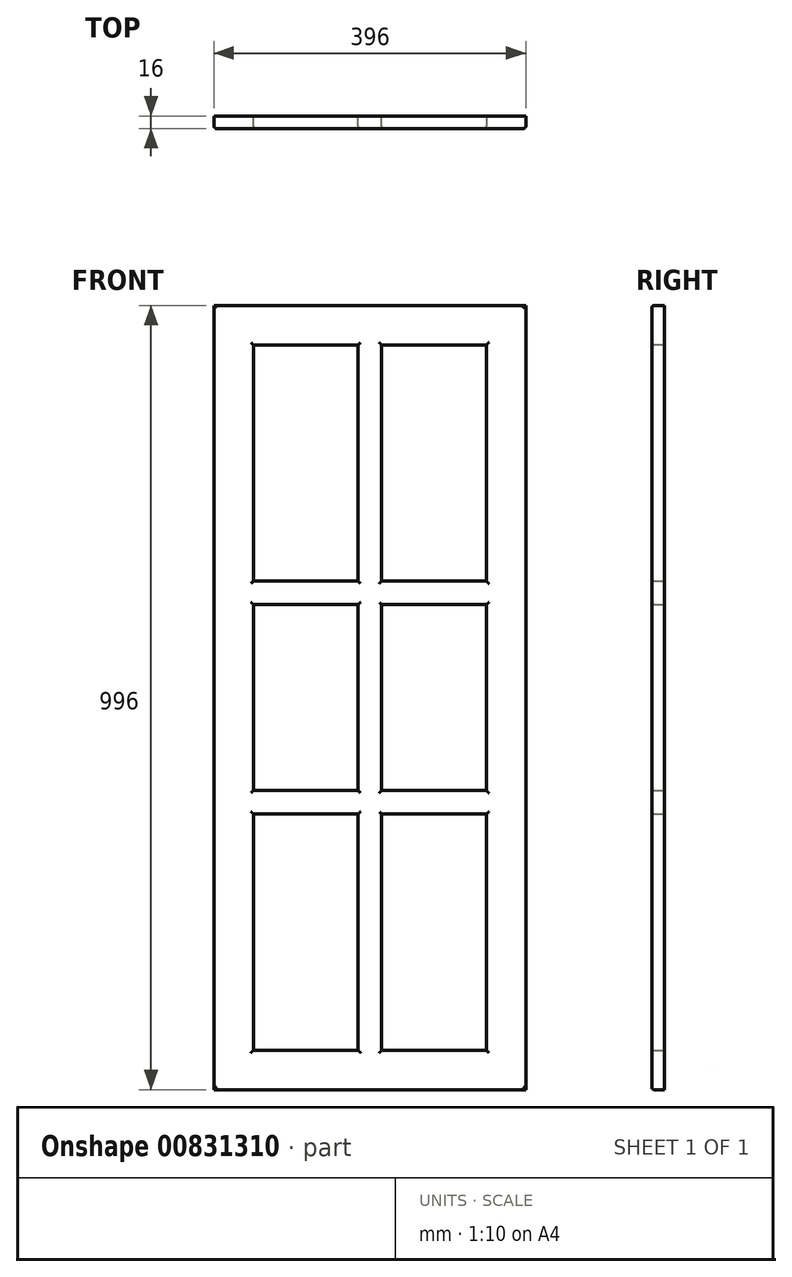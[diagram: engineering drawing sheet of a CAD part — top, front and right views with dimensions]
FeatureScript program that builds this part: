
annotation { "Feature Type Name" : "Feature", "Feature Type Description" : "" }
export const myFeature = defineFeature(function(context is Context, id is Id, definition is map)
    precondition{}
    {
        {
            var Q0;
            Q0=qCreatedBy(makeId("Front.planeOp"),FACE);
            var sketch = newSketch(context, id + "F0", { "sketchPlane" : qUnion([Q0])});
            skLineSegment(sketch, "E0.bottom", {"start": v(0, 0) * mm, "end": v(28.85, 0) * mm});
            skLineSegment(sketch, "E0.top", {"start": v(0, 37.88) * mm, "end": v(28.85, 37.88) * mm});
            skLineSegment(sketch, "E0.left", {"start": v(0, 0) * mm, "end": v(0, 37.88) * mm});
            skLineSegment(sketch, "E0.right", {"start": v(28.85, 0) * mm, "end": v(28.85, 37.88) * mm});
            skSolve(sketch);
        }
        {
            var Q0;
            Q0=makeQuery(id+"F0.imprint","IMPRINT",FACE,{"disambiguationData":[TD([[makeQuery(id+"F0.imprint","IMPRINT",EDGE,{"derivedFrom":sQuery(id+"F0.wireOp",EDGE,"E0.bottom")}),1.0]])]});
            extrude(context, id + "F1", {"entities" : qUnion([Q0]), "depth" : 16 * mm, "offsetDistance" : 25.4 * mm});
        }
        {
            var Q0;
            Q0=makeQuery(id+"F1.opExtrude","SWEPT_FACE",FACE,{"disambiguationData":[OSD([sQuery(id+"F0.wireOp",EDGE,"E0.left")])]});
            extrude(context, id + "F2", {"entities" : qUnion([Q0]), "operationType" : NewBodyOperationType.ADD, "oppositeDirection" : true, "depth" : 296 * mm, "offsetDistance" : 25.4 * mm});
        }
        {
            var Q0;
            {var subQ0=sQuery(id+"F0.wireOp",EDGE,"E0.bottom");Q0=makeQuery(id+"F2.boolean.opBoolean","MERGE",FACE,{"derivedFrom":[makeQuery(id+"F1.opExtrude","SWEPT_FACE",FACE,{"disambiguationData":[OSD([subQ0])]}),makeQuery(id+"F2.opExtrude","SWEPT_FACE",FACE,{"disambiguationData":[OSD([subQ0,sQuery(id+"F0.wireOp",EDGE,"E0.left")])]})]});}
            extrude(context, id + "F3", {"entities" : qUnion([Q0]), "operationType" : NewBodyOperationType.ADD, "oppositeDirection" : true, "depth" : 996 * mm, "offsetDistance" : 25 * mm});
        }
        {
            var Q0;
            {var subQ0=sQuery(id+"F0.wireOp",EDGE,"E0.left");var subQ1=sQuery(id+"F0.wireOp",EDGE,"E0.bottom");Q0=makeQuery(id+"F3.boolean.opBoolean","MERGE",FACE,{"derivedFrom":[makeQuery(id+"F2.boolean.opBoolean","MERGE",FACE,{"derivedFrom":[makeQuery(id+"F1.opExtrude","CAP_FACE",FACE,{"disambiguationData":[OSD([subQ1,sQuery(id+"F0.wireOp",EDGE,"E0.top"),subQ0,sQuery(id+"F0.wireOp",EDGE,"E0.right")])],"isStart":false}),makeQuery(id+"F2.opExtrude","SWEPT_FACE",FACE,{"disambiguationData":[OSD([subQ0]),TDD([makeQuery(id+"F1.opExtrude","CAP_EDGE",EDGE,{"disambiguationData":[OSD([subQ0])],"isStart":false})])]})]}),makeQuery(id+"F3.opExtrude","SWEPT_FACE",FACE,{"disambiguationData":[OSD([subQ1,subQ0]),TDD([makeQuery(id+"F2.boolean.opBoolean","MERGE",EDGE,{"derivedFrom":[makeQuery(id+"F1.opExtrude","CAP_EDGE",EDGE,{"disambiguationData":[OSD([subQ1])],"isStart":false}),makeQuery(id+"F2.opExtrude","SWEPT_EDGE",EDGE,{"disambiguationData":[OSD([subQ1,subQ0]),TDD([makeQuery(id+"F1.opExtrude","CAP_VERTEX",VERTEX,{"disambiguationData":[OSD([subQ1,subQ0])],"isStart":false})])]})]})])]})]});}
            var sketch = newSketch(context, id + "F4", { "sketchPlane" : qUnion([Q0])});
            skLineSegment(sketch, "E1.bottom", {"start": v(48.4, 906.79) * mm, "end": v(248.24, 906.79) * mm});
            skLineSegment(sketch, "E1.top", {"start": v(48.4, 105.66) * mm, "end": v(248.24, 105.66) * mm});
            skLineSegment(sketch, "E1.left", {"start": v(48.4, 906.79) * mm, "end": v(48.4, 105.66) * mm});
            skLineSegment(sketch, "E1.right", {"start": v(248.24, 906.79) * mm, "end": v(248.24, 105.66) * mm});
            skSolve(sketch);
        }
        {
            var Q0;
            Q0=makeQuery(id+"F4.imprint","IMPRINT",FACE,{"disambiguationData":[TD([[makeQuery(id+"F4.imprint","IMPRINT",EDGE,{"derivedFrom":sQuery(id+"F4.wireOp",EDGE,"E1.bottom")}),-1.0]])]});
            extrude(context, id + "F5", {"entities" : qUnion([Q0]), "operationType" : NewBodyOperationType.REMOVE, "oppositeDirection" : true, "depth" : 5 * mm, "offsetDistance" : 25 * mm});
        }
        {
            var Q0;
            Q0=makeQuery(id+"F5.boolean.opBoolean","COPY",FACE,{"derivedFrom":makeQuery(id+"F5.opExtrude","SWEPT_FACE",FACE,{"disambiguationData":[OSD([sQuery(id+"F4.wireOp",EDGE,"E1.bottom")])]})});
            extrude(context, id + "F6", {"entities" : qUnion([Q0]), "operationType" : NewBodyOperationType.REMOVE, "oppositeDirection" : true, "depth" : 39.2 * mm, "offsetDistance" : 25 * mm});
        }
        {
            var Q0;
            {var subQ0=sQuery(id+"F4.wireOp",EDGE,"E1.right");Q0=makeQuery(id+"F6.boolean.opBoolean","MERGE",FACE,{"derivedFrom":[makeQuery(id+"F5.boolean.opBoolean","COPY",FACE,{"derivedFrom":makeQuery(id+"F5.opExtrude","SWEPT_FACE",FACE,{"disambiguationData":[OSD([subQ0])]})}),makeQuery(id+"F6.opExtrude","SWEPT_FACE",FACE,{"disambiguationData":[OSD([sQuery(id+"F4.wireOp",EDGE,"E1.bottom"),subQ0])]})]});}
            extrude(context, id + "F7", {"entities" : qUnion([Q0]), "operationType" : NewBodyOperationType.ADD, "depth" : 2.24 * mm, "offsetDistance" : 25 * mm});
        }
        {
            var Q0;
            Q0=makeQuery(id+"F5.boolean.opBoolean","COPY",FACE,{"derivedFrom":makeQuery(id+"F5.opExtrude","SWEPT_FACE",FACE,{"disambiguationData":[OSD([sQuery(id+"F4.wireOp",EDGE,"E1.top")])]})});
            extrude(context, id + "F8", {"entities" : qUnion([Q0]), "operationType" : NewBodyOperationType.REMOVE, "oppositeDirection" : true, "depth" : 55.66 * mm, "offsetDistance" : 25 * mm});
        }
        {
            var Q0;
            {var subQ0=sQuery(id+"F4.wireOp",EDGE,"E1.left");Q0=makeQuery(id+"F8.boolean.opBoolean","MERGE",FACE,{"derivedFrom":[makeQuery(id+"F6.boolean.opBoolean","MERGE",FACE,{"derivedFrom":[makeQuery(id+"F5.boolean.opBoolean","COPY",FACE,{"derivedFrom":makeQuery(id+"F5.opExtrude","SWEPT_FACE",FACE,{"disambiguationData":[OSD([subQ0])]})}),makeQuery(id+"F6.opExtrude","SWEPT_FACE",FACE,{"disambiguationData":[OSD([sQuery(id+"F4.wireOp",EDGE,"E1.bottom"),subQ0])]})]}),makeQuery(id+"F8.opExtrude","SWEPT_FACE",FACE,{"disambiguationData":[OSD([sQuery(id+"F4.wireOp",EDGE,"E1.top"),subQ0])]})]});}
            extrude(context, id + "F9", {"entities" : qUnion([Q0]), "operationType" : NewBodyOperationType.ADD, "depth" : 1.59 * mm, "offsetDistance" : 25 * mm});
        }
        {
            var Q0;
            {var subQ0=sQuery(id+"F4.wireOp",EDGE,"E1.top");var subQ1=sQuery(id+"F4.wireOp",EDGE,"E1.bottom");Q0=makeQuery(id+"F8.boolean.opBoolean","MERGE",FACE,{"derivedFrom":[makeQuery(id+"F6.boolean.opBoolean","MERGE",FACE,{"derivedFrom":[makeQuery(id+"F5.boolean.opBoolean","COPY",FACE,{"derivedFrom":makeQuery(id+"F5.opExtrude","CAP_FACE",FACE,{"disambiguationData":[OSD([subQ1,subQ0,sQuery(id+"F4.wireOp",EDGE,"E1.left"),sQuery(id+"F4.wireOp",EDGE,"E1.right")])],"isStart":false})}),makeQuery(id+"F6.opExtrude","SWEPT_FACE",FACE,{"disambiguationData":[OSD([subQ1]),TDD([makeQuery(id+"F5.boolean.opBoolean","COPY",EDGE,{"derivedFrom":makeQuery(id+"F5.opExtrude","CAP_EDGE",EDGE,{"disambiguationData":[OSD([subQ1])],"isStart":false})})])]})]}),makeQuery(id+"F8.opExtrude","SWEPT_FACE",FACE,{"disambiguationData":[OSD([subQ0]),TDD([makeQuery(id+"F5.boolean.opBoolean","COPY",EDGE,{"derivedFrom":makeQuery(id+"F5.opExtrude","CAP_EDGE",EDGE,{"disambiguationData":[OSD([subQ0])],"isStart":false})})])]})]});}
            var sketch = newSketch(context, id + "F10", { "sketchPlane" : qUnion([Q0])});
            skLineSegment(sketch, "E2.bottom", {"start": v(127.14, 946) * mm, "end": v(181.91, 946) * mm});
            skLineSegment(sketch, "E2.top", {"start": v(127.14, 50) * mm, "end": v(181.91, 50) * mm});
            skLineSegment(sketch, "E2.left", {"start": v(127.14, 946) * mm, "end": v(127.14, 50) * mm});
            skLineSegment(sketch, "E2.right", {"start": v(181.91, 946) * mm, "end": v(181.91, 50) * mm});
            skSolve(sketch);
        }
        {
            var Q0;
            Q0=makeQuery(id+"F10.imprint","IMPRINT",FACE,{"disambiguationData":[TD([[makeQuery(id+"F10.imprint","IMPRINT",EDGE,{"derivedFrom":sQuery(id+"F10.wireOp",EDGE,"E2.bottom")}),-1.0]])]});
            extrude(context, id + "F11", {"entities" : qUnion([Q0]), "operationType" : NewBodyOperationType.ADD, "depth" : 5 * mm, "offsetDistance" : 25 * mm});
        }
        {
            var Q0;
            Q0=makeQuery(id+"F11.opExtrude","SWEPT_FACE",FACE,{"disambiguationData":[OSD([sQuery(id+"F10.wireOp",EDGE,"E2.left")])]});
            extrude(context, id + "F12", {"entities" : qUnion([Q0]), "operationType" : NewBodyOperationType.REMOVE, "oppositeDirection" : true, "depth" : 5.86 * mm, "offsetDistance" : 25 * mm});
        }
        {
            var Q0;
            Q0=makeQuery(id+"F11.opExtrude","SWEPT_FACE",FACE,{"disambiguationData":[OSD([sQuery(id+"F10.wireOp",EDGE,"E2.right")])]});
            extrude(context, id + "F13", {"entities" : qUnion([Q0]), "operationType" : NewBodyOperationType.REMOVE, "oppositeDirection" : true, "depth" : 18.91 * mm, "offsetDistance" : 25 * mm});
        }
        {
            var Q0;
            {var subQ0=sQuery(id+"F10.wireOp",EDGE,"E2.left");var subQ1=sQuery(id+"F4.wireOp",EDGE,"E1.bottom");var subQ2=sQuery(id+"F4.wireOp",EDGE,"E1.top");var subQ3=sQuery(id+"F4.wireOp",EDGE,"E1.left");Q0=makeQuery(id+"F12.boolean.opBoolean","MERGE",FACE,{"derivedFrom":[makeQuery(id+"F11.boolean.opBoolean","SPLIT",FACE,{"disambiguationData":[TD([makeQuery(id+"F11.opExtrude","SWEPT_FACE",FACE,{"disambiguationData":[OSD([subQ0])]})])],"derivedFrom":makeQuery(id+"F8.boolean.opBoolean","MERGE",FACE,{"derivedFrom":[makeQuery(id+"F6.boolean.opBoolean","MERGE",FACE,{"derivedFrom":[makeQuery(id+"F5.boolean.opBoolean","COPY",FACE,{"derivedFrom":makeQuery(id+"F5.opExtrude","CAP_FACE",FACE,{"disambiguationData":[OSD([subQ1,subQ2,subQ3,sQuery(id+"F4.wireOp",EDGE,"E1.right")])],"isStart":false})}),makeQuery(id+"F6.opExtrude","SWEPT_FACE",FACE,{"disambiguationData":[OSD([subQ1]),TDD([makeQuery(id+"F5.boolean.opBoolean","COPY",EDGE,{"derivedFrom":makeQuery(id+"F5.opExtrude","CAP_EDGE",EDGE,{"disambiguationData":[OSD([subQ1])],"isStart":false})})])]})]}),makeQuery(id+"F8.opExtrude","SWEPT_FACE",FACE,{"disambiguationData":[OSD([subQ2]),TDD([makeQuery(id+"F5.boolean.opBoolean","COPY",EDGE,{"derivedFrom":makeQuery(id+"F5.opExtrude","CAP_EDGE",EDGE,{"disambiguationData":[OSD([subQ2])],"isStart":false})})])]})]})}),makeQuery(id+"F12.opExtrude","SWEPT_FACE",FACE,{"disambiguationData":[OSD([subQ0]),TDD([makeQuery(id+"F11.opExtrude","CAP_EDGE",EDGE,{"disambiguationData":[OSD([subQ0])],"isStart":true})])]})]});}
            var sketch = newSketch(context, id + "F14", { "sketchPlane" : qUnion([Q0])});
            skLineSegment(sketch, "E3.bottom", {"start": v(50, 870.78) * mm, "end": v(133, 870.78) * mm});
            skLineSegment(sketch, "E3.top", {"start": v(50, 835.83) * mm, "end": v(133, 835.83) * mm});
            skLineSegment(sketch, "E3.left", {"start": v(50, 870.78) * mm, "end": v(50, 835.83) * mm});
            skLineSegment(sketch, "E3.right", {"start": v(133, 870.78) * mm, "end": v(133, 835.83) * mm});
            skLineSegment(sketch, "E4.bottom", {"start": v(50, 539.3) * mm, "end": v(133, 539.3) * mm});
            skLineSegment(sketch, "E4.top", {"start": v(50, 484.02) * mm, "end": v(133, 484.02) * mm});
            skLineSegment(sketch, "E4.left", {"start": v(50, 539.3) * mm, "end": v(50, 484.02) * mm});
            skLineSegment(sketch, "E4.right", {"start": v(133, 539.3) * mm, "end": v(133, 484.02) * mm});
            skSolve(sketch);
        }
        {
            var Q0;
            {var subQ0=sQuery(id+"F10.wireOp",EDGE,"E2.right");var subQ1=sQuery(id+"F4.wireOp",EDGE,"E1.top");var subQ2=sQuery(id+"F4.wireOp",EDGE,"E1.right");var subQ3=sQuery(id+"F4.wireOp",EDGE,"E1.bottom");Q0=makeQuery(id+"F13.boolean.opBoolean","MERGE",FACE,{"derivedFrom":[makeQuery(id+"F11.boolean.opBoolean","SPLIT",FACE,{"disambiguationData":[TD([makeQuery(id+"F11.opExtrude","SWEPT_FACE",FACE,{"disambiguationData":[OSD([subQ0])]})])],"derivedFrom":makeQuery(id+"F8.boolean.opBoolean","MERGE",FACE,{"derivedFrom":[makeQuery(id+"F6.boolean.opBoolean","MERGE",FACE,{"derivedFrom":[makeQuery(id+"F5.boolean.opBoolean","COPY",FACE,{"derivedFrom":makeQuery(id+"F5.opExtrude","CAP_FACE",FACE,{"disambiguationData":[OSD([subQ3,subQ1,sQuery(id+"F4.wireOp",EDGE,"E1.left"),subQ2])],"isStart":false})}),makeQuery(id+"F6.opExtrude","SWEPT_FACE",FACE,{"disambiguationData":[OSD([subQ3]),TDD([makeQuery(id+"F5.boolean.opBoolean","COPY",EDGE,{"derivedFrom":makeQuery(id+"F5.opExtrude","CAP_EDGE",EDGE,{"disambiguationData":[OSD([subQ3])],"isStart":false})})])]})]}),makeQuery(id+"F8.opExtrude","SWEPT_FACE",FACE,{"disambiguationData":[OSD([subQ1]),TDD([makeQuery(id+"F5.boolean.opBoolean","COPY",EDGE,{"derivedFrom":makeQuery(id+"F5.opExtrude","CAP_EDGE",EDGE,{"disambiguationData":[OSD([subQ1])],"isStart":false})})])]})]})}),makeQuery(id+"F13.opExtrude","SWEPT_FACE",FACE,{"disambiguationData":[OSD([subQ0]),TDD([makeQuery(id+"F11.opExtrude","CAP_EDGE",EDGE,{"disambiguationData":[OSD([subQ0])],"isStart":true})])]})]});}
            var sketch = newSketch(context, id + "F15", { "sketchPlane" : qUnion([Q0])});
            skLineSegment(sketch, "E5.bottom", {"start": v(163, 876.14) * mm, "end": v(246, 876.14) * mm});
            skLineSegment(sketch, "E5.top", {"start": v(163, 831.26) * mm, "end": v(246, 831.26) * mm});
            skLineSegment(sketch, "E5.left", {"start": v(163, 876.14) * mm, "end": v(163, 831.26) * mm});
            skLineSegment(sketch, "E5.right", {"start": v(246, 876.14) * mm, "end": v(246, 831.26) * mm});
            skLineSegment(sketch, "E6.bottom", {"start": v(163, 602.8) * mm, "end": v(246, 602.8) * mm});
            skLineSegment(sketch, "E6.top", {"start": v(163, 550.28) * mm, "end": v(246, 550.28) * mm});
            skLineSegment(sketch, "E6.left", {"start": v(163, 602.8) * mm, "end": v(163, 550.28) * mm});
            skLineSegment(sketch, "E6.right", {"start": v(246, 602.8) * mm, "end": v(246, 550.28) * mm});
            skSolve(sketch);
        }
        {
            var Q0;
            Q0=makeQuery(id+"F14.imprint","IMPRINT",FACE,{"disambiguationData":[TD([[makeQuery(id+"F14.imprint","IMPRINT",EDGE,{"derivedFrom":sQuery(id+"F14.wireOp",EDGE,"E3.bottom")}),-1.0]])]});
            var Q1;
            Q1=makeQuery(id+"F15.imprint","IMPRINT",FACE,{"disambiguationData":[TD([[makeQuery(id+"F15.imprint","IMPRINT",EDGE,{"derivedFrom":sQuery(id+"F15.wireOp",EDGE,"E5.bottom")}),-1.0]])]});
            var Q2;
            Q2=makeQuery(id+"F15.imprint","IMPRINT",FACE,{"disambiguationData":[TD([[makeQuery(id+"F15.imprint","IMPRINT",EDGE,{"derivedFrom":sQuery(id+"F15.wireOp",EDGE,"E6.bottom")}),-1.0]])]});
            var Q3;
            Q3=makeQuery(id+"F14.imprint","IMPRINT",FACE,{"disambiguationData":[TD([[makeQuery(id+"F14.imprint","IMPRINT",EDGE,{"derivedFrom":sQuery(id+"F14.wireOp",EDGE,"E4.bottom")}),-1.0]])]});
            extrude(context, id + "F16", {"entities" : qUnion([Q0, Q1, Q2, Q3]), "operationType" : NewBodyOperationType.ADD, "depth" : 5 * mm, "offsetDistance" : 25 * mm});
        }
        {
            var Q0;
            Q0=makeQuery(id+"F16.opExtrude","SWEPT_FACE",FACE,{"disambiguationData":[OSD([sQuery(id+"F15.wireOp",EDGE,"E6.top")])]});
            var Q1;
            Q1=makeQuery(id+"F16.opExtrude","SWEPT_FACE",FACE,{"disambiguationData":[OSD([sQuery(id+"F14.wireOp",EDGE,"E4.top")])]});
            extrude(context, id + "F17", {"entities" : qUnion([Q0, Q1]), "operationType" : NewBodyOperationType.ADD, "depth" : 300 * mm, "offsetDistance" : 25 * mm});
        }
        {
            var Q0;
            Q0=makeQuery(id+"F16.opExtrude","SWEPT_FACE",FACE,{"disambiguationData":[OSD([sQuery(id+"F14.wireOp",EDGE,"E4.bottom")])]});
            var Q1;
            Q1=makeQuery(id+"F16.opExtrude","SWEPT_FACE",FACE,{"disambiguationData":[OSD([sQuery(id+"F15.wireOp",EDGE,"E6.bottom")])]});
            extrude(context, id + "F18", {"entities" : qUnion([Q0, Q1]), "operationType" : NewBodyOperationType.REMOVE, "oppositeDirection" : true, "depth" : 300 * mm, "offsetDistance" : 25 * mm});
        }
        {
            var Q0;
            Q0=makeQuery(id+"F16.opExtrude","SWEPT_FACE",FACE,{"disambiguationData":[OSD([sQuery(id+"F14.wireOp",EDGE,"E3.top")])]});
            extrude(context, id + "F19", {"entities" : qUnion([Q0]), "operationType" : NewBodyOperationType.ADD, "depth" : 324.8 * mm, "offsetDistance" : 25 * mm});
        }
        {
            var Q0;
            Q0=makeQuery(id+"F16.opExtrude","SWEPT_FACE",FACE,{"disambiguationData":[OSD([sQuery(id+"F14.wireOp",EDGE,"E3.bottom")])]});
            extrude(context, id + "F20", {"entities" : qUnion([Q0]), "operationType" : NewBodyOperationType.REMOVE, "oppositeDirection" : true, "depth" : 324.8 * mm, "offsetDistance" : 25 * mm});
        }
        {
            var Q0;
            Q0=makeQuery(id+"F18.boolean.opBoolean","COPY",FACE,{"derivedFrom":makeQuery(id+"F18.opExtrude","CAP_FACE",FACE,{"disambiguationData":[OSD([sQuery(id+"F14.wireOp",EDGE,"E4.bottom")])],"isStart":false})});
            extrude(context, id + "F21", {"entities" : qUnion([Q0]), "operationType" : NewBodyOperationType.ADD, "depth" : 250 * mm, "offsetDistance" : 25 * mm});
        }
        {
            var Q0;
            Q0=makeQuery(id+"F17.opExtrude","CAP_FACE",FACE,{"disambiguationData":[OSD([sQuery(id+"F14.wireOp",EDGE,"E4.top")])],"isStart":false});
            extrude(context, id + "F22", {"entities" : qUnion([Q0]), "operationType" : NewBodyOperationType.REMOVE, "oppositeDirection" : true, "depth" : 250 * mm, "offsetDistance" : 25 * mm});
        }
        {
            var Q0;
            Q0=makeQuery(id+"F20.boolean.opBoolean","COPY",FACE,{"derivedFrom":makeQuery(id+"F20.opExtrude","CAP_FACE",FACE,{"disambiguationData":[OSD([sQuery(id+"F14.wireOp",EDGE,"E3.bottom")])],"isStart":false})});
            extrude(context, id + "F23", {"entities" : qUnion([Q0]), "operationType" : NewBodyOperationType.ADD, "depth" : 100 * mm, "offsetDistance" : 25 * mm});
        }
        {
            var Q0;
            Q0=makeQuery(id+"F19.opExtrude","CAP_FACE",FACE,{"disambiguationData":[OSD([sQuery(id+"F14.wireOp",EDGE,"E3.top")])],"isStart":false});
            extrude(context, id + "F24", {"entities" : qUnion([Q0]), "operationType" : NewBodyOperationType.REMOVE, "oppositeDirection" : true, "depth" : 100 * mm, "offsetDistance" : 25 * mm});
        }
        {
            var Q0;
            Q0=makeQuery(id+"F23.opExtrude","CAP_FACE",FACE,{"disambiguationData":[OSD([sQuery(id+"F14.wireOp",EDGE,"E3.bottom")])],"isStart":false});
            extrude(context, id + "F25", {"entities" : qUnion([Q0]), "operationType" : NewBodyOperationType.ADD, "depth" : 50 * mm, "offsetDistance" : 25 * mm});
        }
        {
            var Q0;
            Q0=makeQuery(id+"F24.boolean.opBoolean","COPY",FACE,{"derivedFrom":makeQuery(id+"F24.opExtrude","CAP_FACE",FACE,{"disambiguationData":[OSD([sQuery(id+"F14.wireOp",EDGE,"E3.top")])],"isStart":false})});
            extrude(context, id + "F26", {"entities" : qUnion([Q0]), "operationType" : NewBodyOperationType.REMOVE, "oppositeDirection" : true, "depth" : 50 * mm, "offsetDistance" : 25 * mm});
        }
        {
            var Q0;
            Q0=makeQuery(id+"F22.boolean.opBoolean","COPY",FACE,{"derivedFrom":makeQuery(id+"F22.opExtrude","CAP_FACE",FACE,{"disambiguationData":[OSD([sQuery(id+"F14.wireOp",EDGE,"E4.top")])],"isStart":false})});
            extrude(context, id + "F27", {"entities" : qUnion([Q0]), "operationType" : NewBodyOperationType.ADD, "depth" : 134.02 * mm, "offsetDistance" : 25 * mm});
        }
        {
            var Q0;
            Q0=makeQuery(id+"F27.opExtrude","CAP_FACE",FACE,{"disambiguationData":[OSD([sQuery(id+"F14.wireOp",EDGE,"E4.top")])],"isStart":false});
            extrude(context, id + "F28", {"entities" : qUnion([Q0]), "operationType" : NewBodyOperationType.REMOVE, "oppositeDirection" : true, "depth" : 100 * mm, "offsetDistance" : 25 * mm});
        }
        {
            var Q0;
            Q0=makeQuery(id+"F26.boolean.opBoolean","COPY",FACE,{"derivedFrom":makeQuery(id+"F26.opExtrude","CAP_FACE",FACE,{"disambiguationData":[OSD([sQuery(id+"F14.wireOp",EDGE,"E3.top")])],"isStart":false})});
            extrude(context, id + "F29", {"entities" : qUnion([Q0]), "operationType" : NewBodyOperationType.ADD, "depth" : 100 * mm, "offsetDistance" : 25 * mm});
        }
        {
            var Q0;
            Q0=makeQuery(id+"F25.opExtrude","CAP_FACE",FACE,{"disambiguationData":[OSD([sQuery(id+"F14.wireOp",EDGE,"E3.bottom")])],"isStart":false});
            extrude(context, id + "F30", {"entities" : qUnion([Q0]), "operationType" : NewBodyOperationType.REMOVE, "oppositeDirection" : true, "depth" : 100 * mm, "offsetDistance" : 25 * mm});
        }
        {
            var Q0;
            Q0=makeQuery(id+"F30.boolean.opBoolean","COPY",FACE,{"derivedFrom":makeQuery(id+"F30.opExtrude","CAP_FACE",FACE,{"disambiguationData":[OSD([sQuery(id+"F14.wireOp",EDGE,"E3.bottom")])],"isStart":false})});
            extrude(context, id + "F31", {"entities" : qUnion([Q0]), "operationType" : NewBodyOperationType.ADD, "depth" : 50 * mm, "offsetDistance" : 25 * mm});
        }
        {
            var Q0;
            Q0=makeQuery(id+"F29.opExtrude","CAP_FACE",FACE,{"disambiguationData":[OSD([sQuery(id+"F14.wireOp",EDGE,"E3.top")])],"isStart":false});
            extrude(context, id + "F32", {"entities" : qUnion([Q0]), "operationType" : NewBodyOperationType.REMOVE, "oppositeDirection" : true, "depth" : 54.95 * mm, "offsetDistance" : 25 * mm});
        }
        {
            var Q0;
            Q0=makeQuery(id+"F28.boolean.opBoolean","COPY",FACE,{"derivedFrom":makeQuery(id+"F28.opExtrude","CAP_FACE",FACE,{"disambiguationData":[OSD([sQuery(id+"F14.wireOp",EDGE,"E4.top")])],"isStart":false})});
            extrude(context, id + "F33", {"entities" : qUnion([Q0]), "operationType" : NewBodyOperationType.ADD, "depth" : 50 * mm, "offsetDistance" : 25 * mm});
        }
        {
            var Q0;
            Q0=makeQuery(id+"F21.opExtrude","CAP_FACE",FACE,{"disambiguationData":[OSD([sQuery(id+"F14.wireOp",EDGE,"E4.bottom")])],"isStart":false});
            extrude(context, id + "F34", {"entities" : qUnion([Q0]), "operationType" : NewBodyOperationType.REMOVE, "oppositeDirection" : true, "depth" : 109.3 * mm, "offsetDistance" : 25 * mm});
        }
        {
            var Q0;
            Q0=makeQuery(id+"F16.opExtrude","SWEPT_FACE",FACE,{"disambiguationData":[OSD([sQuery(id+"F15.wireOp",EDGE,"E5.top")])]});
            extrude(context, id + "F35", {"entities" : qUnion([Q0]), "operationType" : NewBodyOperationType.REMOVE, "oppositeDirection" : true, "depth" : 14.88 * mm, "offsetDistance" : 25 * mm});
        }
        {
            var Q0;
            Q0=makeQuery(id+"F35.boolean.opBoolean","COPY",FACE,{"derivedFrom":makeQuery(id+"F35.opExtrude","CAP_FACE",FACE,{"disambiguationData":[OSD([sQuery(id+"F15.wireOp",EDGE,"E5.top")])],"isStart":false})});
            extrude(context, id + "F36", {"entities" : qUnion([Q0]), "operationType" : NewBodyOperationType.ADD, "depth" : 230.15 * mm, "offsetDistance" : 25 * mm});
        }
        {
            var Q0;
            Q0=makeQuery(id+"F16.opExtrude","SWEPT_FACE",FACE,{"disambiguationData":[OSD([sQuery(id+"F15.wireOp",EDGE,"E5.bottom")])]});
            extrude(context, id + "F37", {"entities" : qUnion([Q0]), "operationType" : NewBodyOperationType.REMOVE, "oppositeDirection" : true, "depth" : 230.15 * mm, "offsetDistance" : 25 * mm});
        }
        {
            var Q0;
            Q0=makeQuery(id+"F17.opExtrude","CAP_FACE",FACE,{"disambiguationData":[OSD([sQuery(id+"F15.wireOp",EDGE,"E6.top")])],"isStart":false});
            extrude(context, id + "F38", {"entities" : qUnion([Q0]), "operationType" : NewBodyOperationType.REMOVE, "oppositeDirection" : true, "depth" : 22.52 * mm, "offsetDistance" : 25 * mm});
        }
        {
            var Q0;
            Q0=makeQuery(id+"F18.boolean.opBoolean","COPY",FACE,{"derivedFrom":makeQuery(id+"F18.opExtrude","CAP_FACE",FACE,{"disambiguationData":[OSD([sQuery(id+"F15.wireOp",EDGE,"E6.bottom")])],"isStart":false})});
            extrude(context, id + "F39", {"entities" : qUnion([Q0]), "operationType" : NewBodyOperationType.ADD, "depth" : 77.2 * mm, "offsetDistance" : 25 * mm});
        }
        {
            var Q0;
            Q0=makeQuery(id+"F38.boolean.opBoolean","COPY",FACE,{"derivedFrom":makeQuery(id+"F38.opExtrude","CAP_FACE",FACE,{"disambiguationData":[OSD([sQuery(id+"F15.wireOp",EDGE,"E6.top")])],"isStart":false})});
            extrude(context, id + "F40", {"entities" : qUnion([Q0]), "operationType" : NewBodyOperationType.REMOVE, "oppositeDirection" : true, "depth" : 77.2 * mm, "offsetDistance" : 25 * mm});
        }
        {
            var Q0;
            {var subQ0=sQuery(id+"F14.wireOp",EDGE,"E3.bottom");var subQ1=makeQuery(id+"F16.opExtrude","CAP_EDGE",EDGE,{"disambiguationData":[OSD([subQ0])],"isStart":true});var subQ2=sQuery(id+"F10.wireOp",EDGE,"E2.left");var subQ3=sQuery(id+"F4.wireOp",EDGE,"E1.bottom");var subQ4=sQuery(id+"F4.wireOp",EDGE,"E1.left");var subQ5=sQuery(id+"F4.wireOp",EDGE,"E1.top");var subQ7=makeQuery(id+"F6.boolean.opBoolean","COPY",FACE,{"derivedFrom":makeQuery(id+"F6.opExtrude","CAP_FACE",FACE,{"disambiguationData":[OSD([subQ3])],"isStart":false})});Q0=makeQuery(id+"F30.boolean.opBoolean","MERGE",FACE,{"derivedFrom":[makeQuery(id+"F20.boolean.opBoolean","MERGE",FACE,{"derivedFrom":[makeQuery(id+"F16.boolean.opBoolean","SPLIT",FACE,{"disambiguationData":[TD([subQ7])],"derivedFrom":makeQuery(id+"F12.boolean.opBoolean","MERGE",FACE,{"derivedFrom":[makeQuery(id+"F11.boolean.opBoolean","SPLIT",FACE,{"disambiguationData":[TD([makeQuery(id+"F11.opExtrude","SWEPT_FACE",FACE,{"disambiguationData":[OSD([subQ2])]})])],"derivedFrom":makeQuery(id+"F8.boolean.opBoolean","MERGE",FACE,{"derivedFrom":[makeQuery(id+"F6.boolean.opBoolean","MERGE",FACE,{"derivedFrom":[makeQuery(id+"F5.boolean.opBoolean","COPY",FACE,{"derivedFrom":makeQuery(id+"F5.opExtrude","CAP_FACE",FACE,{"disambiguationData":[OSD([subQ3,subQ5,subQ4,sQuery(id+"F4.wireOp",EDGE,"E1.right")])],"isStart":false})}),makeQuery(id+"F6.opExtrude","SWEPT_FACE",FACE,{"disambiguationData":[OSD([subQ3]),TDD([makeQuery(id+"F5.boolean.opBoolean","COPY",EDGE,{"derivedFrom":makeQuery(id+"F5.opExtrude","CAP_EDGE",EDGE,{"disambiguationData":[OSD([subQ3])],"isStart":false})})])]})]}),makeQuery(id+"F8.opExtrude","SWEPT_FACE",FACE,{"disambiguationData":[OSD([subQ5]),TDD([makeQuery(id+"F5.boolean.opBoolean","COPY",EDGE,{"derivedFrom":makeQuery(id+"F5.opExtrude","CAP_EDGE",EDGE,{"disambiguationData":[OSD([subQ5])],"isStart":false})})])]})]})}),makeQuery(id+"F12.opExtrude","SWEPT_FACE",FACE,{"disambiguationData":[OSD([subQ2]),TDD([makeQuery(id+"F11.opExtrude","CAP_EDGE",EDGE,{"disambiguationData":[OSD([subQ2])],"isStart":true})])]})]})}),makeQuery(id+"F20.opExtrude","SWEPT_FACE",FACE,{"disambiguationData":[OSD([subQ0]),TDD([subQ1])]})]}),makeQuery(id+"F30.opExtrude","SWEPT_FACE",FACE,{"disambiguationData":[OSD([subQ0]),TDD([makeQuery(id+"F25.opExtrude","CAP_EDGE",EDGE,{"disambiguationData":[OSD([subQ0]),TDD([makeQuery(id+"F23.opExtrude","CAP_EDGE",EDGE,{"disambiguationData":[OSD([subQ0]),TDD([makeQuery(id+"F20.boolean.opBoolean","COPY",EDGE,{"derivedFrom":makeQuery(id+"F20.opExtrude","CAP_EDGE",EDGE,{"disambiguationData":[OSD([subQ0]),TDD([subQ1])],"isStart":false})})])],"isStart":false})])],"isStart":false})])]})]});}
            var Q1;
            {var subQ0=sQuery(id+"F15.wireOp",EDGE,"E5.bottom");var subQ1=sQuery(id+"F10.wireOp",EDGE,"E2.right");var subQ2=sQuery(id+"F4.wireOp",EDGE,"E1.bottom");var subQ3=sQuery(id+"F4.wireOp",EDGE,"E1.right");var subQ4=sQuery(id+"F4.wireOp",EDGE,"E1.top");var subQ7=makeQuery(id+"F6.boolean.opBoolean","COPY",FACE,{"derivedFrom":makeQuery(id+"F6.opExtrude","CAP_FACE",FACE,{"disambiguationData":[OSD([subQ2])],"isStart":false})});Q1=makeQuery(id+"F37.boolean.opBoolean","MERGE",FACE,{"derivedFrom":[makeQuery(id+"F16.boolean.opBoolean","SPLIT",FACE,{"disambiguationData":[TD([subQ7])],"derivedFrom":makeQuery(id+"F13.boolean.opBoolean","MERGE",FACE,{"derivedFrom":[makeQuery(id+"F11.boolean.opBoolean","SPLIT",FACE,{"disambiguationData":[TD([makeQuery(id+"F11.opExtrude","SWEPT_FACE",FACE,{"disambiguationData":[OSD([subQ1])]})])],"derivedFrom":makeQuery(id+"F8.boolean.opBoolean","MERGE",FACE,{"derivedFrom":[makeQuery(id+"F6.boolean.opBoolean","MERGE",FACE,{"derivedFrom":[makeQuery(id+"F5.boolean.opBoolean","COPY",FACE,{"derivedFrom":makeQuery(id+"F5.opExtrude","CAP_FACE",FACE,{"disambiguationData":[OSD([subQ2,subQ4,sQuery(id+"F4.wireOp",EDGE,"E1.left"),subQ3])],"isStart":false})}),makeQuery(id+"F6.opExtrude","SWEPT_FACE",FACE,{"disambiguationData":[OSD([subQ2]),TDD([makeQuery(id+"F5.boolean.opBoolean","COPY",EDGE,{"derivedFrom":makeQuery(id+"F5.opExtrude","CAP_EDGE",EDGE,{"disambiguationData":[OSD([subQ2])],"isStart":false})})])]})]}),makeQuery(id+"F8.opExtrude","SWEPT_FACE",FACE,{"disambiguationData":[OSD([subQ4]),TDD([makeQuery(id+"F5.boolean.opBoolean","COPY",EDGE,{"derivedFrom":makeQuery(id+"F5.opExtrude","CAP_EDGE",EDGE,{"disambiguationData":[OSD([subQ4])],"isStart":false})})])]})]})}),makeQuery(id+"F13.opExtrude","SWEPT_FACE",FACE,{"disambiguationData":[OSD([subQ1]),TDD([makeQuery(id+"F11.opExtrude","CAP_EDGE",EDGE,{"disambiguationData":[OSD([subQ1])],"isStart":true})])]})]})}),makeQuery(id+"F37.opExtrude","SWEPT_FACE",FACE,{"disambiguationData":[OSD([subQ0]),TDD([makeQuery(id+"F16.opExtrude","CAP_EDGE",EDGE,{"disambiguationData":[OSD([subQ0])],"isStart":true})])]})]});}
            var Q2;
            {var subQ0=sQuery(id+"F15.wireOp",EDGE,"E5.top");var subQ1=sQuery(id+"F15.wireOp",EDGE,"E6.bottom");var subQ2=sQuery(id+"F10.wireOp",EDGE,"E2.right");var subQ3=sQuery(id+"F4.wireOp",EDGE,"E1.right");var subQ4=sQuery(id+"F4.wireOp",EDGE,"E1.top");var subQ6=sQuery(id+"F4.wireOp",EDGE,"E1.bottom");Q2=makeQuery(id+"F35.boolean.opBoolean","MERGE",FACE,{"derivedFrom":[makeQuery(id+"F18.boolean.opBoolean","MERGE",FACE,{"derivedFrom":[makeQuery(id+"F16.boolean.opBoolean","SPLIT",FACE,{"disambiguationData":[TD([makeQuery(id+"F16.opExtrude","SWEPT_FACE",FACE,{"disambiguationData":[OSD([subQ0])]})])],"derivedFrom":makeQuery(id+"F13.boolean.opBoolean","MERGE",FACE,{"derivedFrom":[makeQuery(id+"F11.boolean.opBoolean","SPLIT",FACE,{"disambiguationData":[TD([makeQuery(id+"F11.opExtrude","SWEPT_FACE",FACE,{"disambiguationData":[OSD([subQ2])]})])],"derivedFrom":makeQuery(id+"F8.boolean.opBoolean","MERGE",FACE,{"derivedFrom":[makeQuery(id+"F6.boolean.opBoolean","MERGE",FACE,{"derivedFrom":[makeQuery(id+"F5.boolean.opBoolean","COPY",FACE,{"derivedFrom":makeQuery(id+"F5.opExtrude","CAP_FACE",FACE,{"disambiguationData":[OSD([subQ6,subQ4,sQuery(id+"F4.wireOp",EDGE,"E1.left"),subQ3])],"isStart":false})}),makeQuery(id+"F6.opExtrude","SWEPT_FACE",FACE,{"disambiguationData":[OSD([subQ6]),TDD([makeQuery(id+"F5.boolean.opBoolean","COPY",EDGE,{"derivedFrom":makeQuery(id+"F5.opExtrude","CAP_EDGE",EDGE,{"disambiguationData":[OSD([subQ6])],"isStart":false})})])]})]}),makeQuery(id+"F8.opExtrude","SWEPT_FACE",FACE,{"disambiguationData":[OSD([subQ4]),TDD([makeQuery(id+"F5.boolean.opBoolean","COPY",EDGE,{"derivedFrom":makeQuery(id+"F5.opExtrude","CAP_EDGE",EDGE,{"disambiguationData":[OSD([subQ4])],"isStart":false})})])]})]})}),makeQuery(id+"F13.opExtrude","SWEPT_FACE",FACE,{"disambiguationData":[OSD([subQ2]),TDD([makeQuery(id+"F11.opExtrude","CAP_EDGE",EDGE,{"disambiguationData":[OSD([subQ2])],"isStart":true})])]})]})}),makeQuery(id+"F18.opExtrude","SWEPT_FACE",FACE,{"disambiguationData":[OSD([subQ1]),TDD([makeQuery(id+"F16.opExtrude","CAP_EDGE",EDGE,{"disambiguationData":[OSD([subQ1])],"isStart":true})])]})]}),makeQuery(id+"F35.opExtrude","SWEPT_FACE",FACE,{"disambiguationData":[OSD([subQ0]),TDD([makeQuery(id+"F16.opExtrude","CAP_EDGE",EDGE,{"disambiguationData":[OSD([subQ0])],"isStart":true})])]})]});}
            var Q3;
            {var subQ0=sQuery(id+"F14.wireOp",EDGE,"E4.bottom");var subQ1=makeQuery(id+"F16.opExtrude","CAP_EDGE",EDGE,{"disambiguationData":[OSD([subQ0])],"isStart":true});var subQ2=sQuery(id+"F14.wireOp",EDGE,"E3.top");var subQ3=makeQuery(id+"F19.opExtrude","CAP_EDGE",EDGE,{"disambiguationData":[OSD([subQ2]),TDD([makeQuery(id+"F16.opExtrude","CAP_EDGE",EDGE,{"disambiguationData":[OSD([subQ2])],"isStart":true})])],"isStart":false});var subQ4=makeQuery(id+"F24.boolean.opBoolean","COPY",EDGE,{"derivedFrom":makeQuery(id+"F24.opExtrude","CAP_EDGE",EDGE,{"disambiguationData":[OSD([subQ2]),TDD([subQ3])],"isStart":false})});var subQ5=sQuery(id+"F4.wireOp",EDGE,"E1.left");var subQ6=sQuery(id+"F4.wireOp",EDGE,"E1.top");var subQ7=sQuery(id+"F4.wireOp",EDGE,"E1.bottom");var subQ9=sQuery(id+"F10.wireOp",EDGE,"E2.left");Q3=makeQuery(id+"F34.boolean.opBoolean","MERGE",FACE,{"derivedFrom":[makeQuery(id+"F32.boolean.opBoolean","MERGE",FACE,{"derivedFrom":[makeQuery(id+"F26.boolean.opBoolean","MERGE",FACE,{"derivedFrom":[makeQuery(id+"F24.boolean.opBoolean","MERGE",FACE,{"derivedFrom":[makeQuery(id+"F18.boolean.opBoolean","MERGE",FACE,{"derivedFrom":[makeQuery(id+"F16.boolean.opBoolean","SPLIT",FACE,{"disambiguationData":[TD([makeQuery(id+"F16.opExtrude","SWEPT_FACE",FACE,{"disambiguationData":[OSD([subQ2])]})])],"derivedFrom":makeQuery(id+"F12.boolean.opBoolean","MERGE",FACE,{"derivedFrom":[makeQuery(id+"F11.boolean.opBoolean","SPLIT",FACE,{"disambiguationData":[TD([makeQuery(id+"F11.opExtrude","SWEPT_FACE",FACE,{"disambiguationData":[OSD([subQ9])]})])],"derivedFrom":makeQuery(id+"F8.boolean.opBoolean","MERGE",FACE,{"derivedFrom":[makeQuery(id+"F6.boolean.opBoolean","MERGE",FACE,{"derivedFrom":[makeQuery(id+"F5.boolean.opBoolean","COPY",FACE,{"derivedFrom":makeQuery(id+"F5.opExtrude","CAP_FACE",FACE,{"disambiguationData":[OSD([subQ7,subQ6,subQ5,sQuery(id+"F4.wireOp",EDGE,"E1.right")])],"isStart":false})}),makeQuery(id+"F6.opExtrude","SWEPT_FACE",FACE,{"disambiguationData":[OSD([subQ7]),TDD([makeQuery(id+"F5.boolean.opBoolean","COPY",EDGE,{"derivedFrom":makeQuery(id+"F5.opExtrude","CAP_EDGE",EDGE,{"disambiguationData":[OSD([subQ7])],"isStart":false})})])]})]}),makeQuery(id+"F8.opExtrude","SWEPT_FACE",FACE,{"disambiguationData":[OSD([subQ6]),TDD([makeQuery(id+"F5.boolean.opBoolean","COPY",EDGE,{"derivedFrom":makeQuery(id+"F5.opExtrude","CAP_EDGE",EDGE,{"disambiguationData":[OSD([subQ6])],"isStart":false})})])]})]})}),makeQuery(id+"F12.opExtrude","SWEPT_FACE",FACE,{"disambiguationData":[OSD([subQ9]),TDD([makeQuery(id+"F11.opExtrude","CAP_EDGE",EDGE,{"disambiguationData":[OSD([subQ9])],"isStart":true})])]})]})}),makeQuery(id+"F18.opExtrude","SWEPT_FACE",FACE,{"disambiguationData":[OSD([subQ0]),TDD([subQ1])]})]}),makeQuery(id+"F24.opExtrude","SWEPT_FACE",FACE,{"disambiguationData":[OSD([subQ2]),TDD([subQ3])]})]}),makeQuery(id+"F26.opExtrude","SWEPT_FACE",FACE,{"disambiguationData":[OSD([subQ2]),TDD([subQ4])]})]}),makeQuery(id+"F32.opExtrude","SWEPT_FACE",FACE,{"disambiguationData":[OSD([subQ2]),TDD([makeQuery(id+"F29.opExtrude","CAP_EDGE",EDGE,{"disambiguationData":[OSD([subQ2]),TDD([makeQuery(id+"F26.boolean.opBoolean","COPY",EDGE,{"derivedFrom":makeQuery(id+"F26.opExtrude","CAP_EDGE",EDGE,{"disambiguationData":[OSD([subQ2]),TDD([subQ4])],"isStart":false})})])],"isStart":false})])]})]}),makeQuery(id+"F34.opExtrude","SWEPT_FACE",FACE,{"disambiguationData":[OSD([subQ0]),TDD([makeQuery(id+"F21.opExtrude","CAP_EDGE",EDGE,{"disambiguationData":[OSD([subQ0]),TDD([makeQuery(id+"F18.boolean.opBoolean","COPY",EDGE,{"derivedFrom":makeQuery(id+"F18.opExtrude","CAP_EDGE",EDGE,{"disambiguationData":[OSD([subQ0]),TDD([subQ1])],"isStart":false})})])],"isStart":false})])]})]});}
            var Q4;
            {var subQ0=sQuery(id+"F14.wireOp",EDGE,"E4.top");var subQ1=makeQuery(id+"F17.opExtrude","CAP_EDGE",EDGE,{"disambiguationData":[OSD([subQ0]),TDD([makeQuery(id+"F16.opExtrude","CAP_EDGE",EDGE,{"disambiguationData":[OSD([subQ0])],"isStart":true})])],"isStart":false});var subQ2=sQuery(id+"F10.wireOp",EDGE,"E2.left");var subQ3=sQuery(id+"F4.wireOp",EDGE,"E1.top");var subQ4=sQuery(id+"F4.wireOp",EDGE,"E1.left");var subQ5=sQuery(id+"F4.wireOp",EDGE,"E1.bottom");var subQ7=makeQuery(id+"F8.boolean.opBoolean","COPY",FACE,{"derivedFrom":makeQuery(id+"F8.opExtrude","CAP_FACE",FACE,{"disambiguationData":[OSD([subQ3])],"isStart":false})});Q4=makeQuery(id+"F28.boolean.opBoolean","MERGE",FACE,{"derivedFrom":[makeQuery(id+"F22.boolean.opBoolean","MERGE",FACE,{"derivedFrom":[makeQuery(id+"F16.boolean.opBoolean","SPLIT",FACE,{"disambiguationData":[TD([subQ7])],"derivedFrom":makeQuery(id+"F12.boolean.opBoolean","MERGE",FACE,{"derivedFrom":[makeQuery(id+"F11.boolean.opBoolean","SPLIT",FACE,{"disambiguationData":[TD([makeQuery(id+"F11.opExtrude","SWEPT_FACE",FACE,{"disambiguationData":[OSD([subQ2])]})])],"derivedFrom":makeQuery(id+"F8.boolean.opBoolean","MERGE",FACE,{"derivedFrom":[makeQuery(id+"F6.boolean.opBoolean","MERGE",FACE,{"derivedFrom":[makeQuery(id+"F5.boolean.opBoolean","COPY",FACE,{"derivedFrom":makeQuery(id+"F5.opExtrude","CAP_FACE",FACE,{"disambiguationData":[OSD([subQ5,subQ3,subQ4,sQuery(id+"F4.wireOp",EDGE,"E1.right")])],"isStart":false})}),makeQuery(id+"F6.opExtrude","SWEPT_FACE",FACE,{"disambiguationData":[OSD([subQ5]),TDD([makeQuery(id+"F5.boolean.opBoolean","COPY",EDGE,{"derivedFrom":makeQuery(id+"F5.opExtrude","CAP_EDGE",EDGE,{"disambiguationData":[OSD([subQ5])],"isStart":false})})])]})]}),makeQuery(id+"F8.opExtrude","SWEPT_FACE",FACE,{"disambiguationData":[OSD([subQ3]),TDD([makeQuery(id+"F5.boolean.opBoolean","COPY",EDGE,{"derivedFrom":makeQuery(id+"F5.opExtrude","CAP_EDGE",EDGE,{"disambiguationData":[OSD([subQ3])],"isStart":false})})])]})]})}),makeQuery(id+"F12.opExtrude","SWEPT_FACE",FACE,{"disambiguationData":[OSD([subQ2]),TDD([makeQuery(id+"F11.opExtrude","CAP_EDGE",EDGE,{"disambiguationData":[OSD([subQ2])],"isStart":true})])]})]})}),makeQuery(id+"F22.opExtrude","SWEPT_FACE",FACE,{"disambiguationData":[OSD([subQ0]),TDD([subQ1])]})]}),makeQuery(id+"F28.opExtrude","SWEPT_FACE",FACE,{"disambiguationData":[OSD([subQ0]),TDD([makeQuery(id+"F27.opExtrude","CAP_EDGE",EDGE,{"disambiguationData":[OSD([subQ0]),TDD([makeQuery(id+"F22.boolean.opBoolean","COPY",EDGE,{"derivedFrom":makeQuery(id+"F22.opExtrude","CAP_EDGE",EDGE,{"disambiguationData":[OSD([subQ0]),TDD([subQ1])],"isStart":false})})])],"isStart":false})])]})]});}
            var Q5;
            {var subQ0=sQuery(id+"F15.wireOp",EDGE,"E6.top");var subQ1=makeQuery(id+"F17.opExtrude","CAP_EDGE",EDGE,{"disambiguationData":[OSD([subQ0]),TDD([makeQuery(id+"F16.opExtrude","CAP_EDGE",EDGE,{"disambiguationData":[OSD([subQ0])],"isStart":true})])],"isStart":false});var subQ2=sQuery(id+"F10.wireOp",EDGE,"E2.right");var subQ3=sQuery(id+"F4.wireOp",EDGE,"E1.top");var subQ4=makeQuery(id+"F8.boolean.opBoolean","COPY",FACE,{"derivedFrom":makeQuery(id+"F8.opExtrude","CAP_FACE",FACE,{"disambiguationData":[OSD([subQ3])],"isStart":false})});var subQ5=sQuery(id+"F4.wireOp",EDGE,"E1.right");var subQ7=sQuery(id+"F4.wireOp",EDGE,"E1.bottom");Q5=makeQuery(id+"F40.boolean.opBoolean","MERGE",FACE,{"derivedFrom":[makeQuery(id+"F38.boolean.opBoolean","MERGE",FACE,{"derivedFrom":[makeQuery(id+"F16.boolean.opBoolean","SPLIT",FACE,{"disambiguationData":[TD([subQ4])],"derivedFrom":makeQuery(id+"F13.boolean.opBoolean","MERGE",FACE,{"derivedFrom":[makeQuery(id+"F11.boolean.opBoolean","SPLIT",FACE,{"disambiguationData":[TD([makeQuery(id+"F11.opExtrude","SWEPT_FACE",FACE,{"disambiguationData":[OSD([subQ2])]})])],"derivedFrom":makeQuery(id+"F8.boolean.opBoolean","MERGE",FACE,{"derivedFrom":[makeQuery(id+"F6.boolean.opBoolean","MERGE",FACE,{"derivedFrom":[makeQuery(id+"F5.boolean.opBoolean","COPY",FACE,{"derivedFrom":makeQuery(id+"F5.opExtrude","CAP_FACE",FACE,{"disambiguationData":[OSD([subQ7,subQ3,sQuery(id+"F4.wireOp",EDGE,"E1.left"),subQ5])],"isStart":false})}),makeQuery(id+"F6.opExtrude","SWEPT_FACE",FACE,{"disambiguationData":[OSD([subQ7]),TDD([makeQuery(id+"F5.boolean.opBoolean","COPY",EDGE,{"derivedFrom":makeQuery(id+"F5.opExtrude","CAP_EDGE",EDGE,{"disambiguationData":[OSD([subQ7])],"isStart":false})})])]})]}),makeQuery(id+"F8.opExtrude","SWEPT_FACE",FACE,{"disambiguationData":[OSD([subQ3]),TDD([makeQuery(id+"F5.boolean.opBoolean","COPY",EDGE,{"derivedFrom":makeQuery(id+"F5.opExtrude","CAP_EDGE",EDGE,{"disambiguationData":[OSD([subQ3])],"isStart":false})})])]})]})}),makeQuery(id+"F13.opExtrude","SWEPT_FACE",FACE,{"disambiguationData":[OSD([subQ2]),TDD([makeQuery(id+"F11.opExtrude","CAP_EDGE",EDGE,{"disambiguationData":[OSD([subQ2])],"isStart":true})])]})]})}),makeQuery(id+"F38.opExtrude","SWEPT_FACE",FACE,{"disambiguationData":[OSD([subQ0]),TDD([subQ1])]})]}),makeQuery(id+"F40.opExtrude","SWEPT_FACE",FACE,{"disambiguationData":[OSD([subQ0]),TDD([makeQuery(id+"F38.boolean.opBoolean","COPY",EDGE,{"derivedFrom":makeQuery(id+"F38.opExtrude","CAP_EDGE",EDGE,{"disambiguationData":[OSD([subQ0]),TDD([subQ1])],"isStart":false})})])]})]});}
            extrude(context, id + "F41", {"entities" : qUnion([Q0, Q1, Q2, Q3, Q4, Q5]), "operationType" : NewBodyOperationType.REMOVE, "oppositeDirection" : true, "depth" : 11 * mm, "offsetDistance" : 25 * mm});
        }
        {
            var Q0;
            {var subQ0=sQuery(id+"F0.wireOp",EDGE,"E0.left");var subQ1=sQuery(id+"F0.wireOp",EDGE,"E0.bottom");Q0=makeQuery(id+"F3.boolean.opBoolean","MERGE",FACE,{"derivedFrom":[makeQuery(id+"F2.opExtrude","CAP_FACE",FACE,{"disambiguationData":[OSD([subQ0])],"isStart":false}),makeQuery(id+"F3.opExtrude","SWEPT_FACE",FACE,{"disambiguationData":[OSD([subQ1,subQ0]),TDD([makeQuery(id+"F2.opExtrude","CAP_EDGE",EDGE,{"disambiguationData":[OSD([subQ1,subQ0])],"isStart":false})])]})]});}
            extrude(context, id + "F42", {"entities" : qUnion([Q0]), "operationType" : NewBodyOperationType.ADD, "depth" : 100 * mm, "offsetDistance" : 25 * mm});
        }
        {
            var Q0;
            {var subQ0=sQuery(id+"F15.wireOp",EDGE,"E5.right");var subQ1=sQuery(id+"F15.wireOp",EDGE,"E5.bottom");var subQ2=sQuery(id+"F4.wireOp",EDGE,"E1.right");var subQ3=sQuery(id+"F4.wireOp",EDGE,"E1.top");var subQ4=sQuery(id+"F4.wireOp",EDGE,"E1.bottom");Q0=makeQuery(id+"F41.boolean.opBoolean","MERGE",FACE,{"derivedFrom":[makeQuery(id+"F37.boolean.opBoolean","MERGE",FACE,{"derivedFrom":[makeQuery(id+"F16.boolean.opBoolean","SPLIT",FACE,{"disambiguationData":[TD([makeQuery(id+"F6.boolean.opBoolean","COPY",FACE,{"derivedFrom":makeQuery(id+"F6.opExtrude","CAP_FACE",FACE,{"disambiguationData":[OSD([subQ4])],"isStart":false})})])],"derivedFrom":makeQuery(id+"F8.boolean.opBoolean","MERGE",FACE,{"derivedFrom":[makeQuery(id+"F7.opExtrude","CAP_FACE",FACE,{"disambiguationData":[OSD([subQ4,subQ2])],"isStart":false}),makeQuery(id+"F8.opExtrude","SWEPT_FACE",FACE,{"disambiguationData":[OSD([subQ3,subQ2])]})]})}),makeQuery(id+"F37.opExtrude","SWEPT_FACE",FACE,{"disambiguationData":[OSD([subQ4,subQ3,subQ2,subQ1,subQ0])]})]}),makeQuery(id+"F41.opExtrude","SWEPT_FACE",FACE,{"disambiguationData":[OSD([subQ4,subQ3,subQ2,subQ1,subQ0])]})]});}
            var Q1;
            {var subQ0=sQuery(id+"F15.wireOp",EDGE,"E6.right");var subQ1=sQuery(id+"F15.wireOp",EDGE,"E6.bottom");var subQ2=sQuery(id+"F15.wireOp",EDGE,"E5.right");var subQ3=sQuery(id+"F15.wireOp",EDGE,"E5.top");var subQ4=sQuery(id+"F4.wireOp",EDGE,"E1.right");var subQ5=sQuery(id+"F4.wireOp",EDGE,"E1.top");var subQ6=sQuery(id+"F4.wireOp",EDGE,"E1.bottom");Q1=makeQuery(id+"F41.boolean.opBoolean","MERGE",FACE,{"derivedFrom":[makeQuery(id+"F35.boolean.opBoolean","MERGE",FACE,{"derivedFrom":[makeQuery(id+"F18.boolean.opBoolean","MERGE",FACE,{"derivedFrom":[makeQuery(id+"F16.boolean.opBoolean","SPLIT",FACE,{"disambiguationData":[TD([makeQuery(id+"F16.opExtrude","SWEPT_FACE",FACE,{"disambiguationData":[OSD([subQ3])]})])],"derivedFrom":makeQuery(id+"F8.boolean.opBoolean","MERGE",FACE,{"derivedFrom":[makeQuery(id+"F7.opExtrude","CAP_FACE",FACE,{"disambiguationData":[OSD([subQ6,subQ4])],"isStart":false}),makeQuery(id+"F8.opExtrude","SWEPT_FACE",FACE,{"disambiguationData":[OSD([subQ5,subQ4])]})]})}),makeQuery(id+"F18.opExtrude","SWEPT_FACE",FACE,{"disambiguationData":[OSD([subQ6,subQ5,subQ4,subQ1,subQ0])]})]}),makeQuery(id+"F35.opExtrude","SWEPT_FACE",FACE,{"disambiguationData":[OSD([subQ6,subQ5,subQ4,subQ3,subQ2])]})]}),makeQuery(id+"F41.opExtrude","SWEPT_FACE",FACE,{"disambiguationData":[OSD([subQ6,subQ5,subQ4,subQ3,subQ2,subQ1,subQ0])]})]});}
            var Q2;
            {var subQ0=sQuery(id+"F15.wireOp",EDGE,"E6.right");var subQ1=sQuery(id+"F15.wireOp",EDGE,"E6.top");var subQ2=sQuery(id+"F4.wireOp",EDGE,"E1.right");var subQ3=sQuery(id+"F4.wireOp",EDGE,"E1.top");var subQ4=sQuery(id+"F4.wireOp",EDGE,"E1.bottom");Q2=makeQuery(id+"F41.boolean.opBoolean","MERGE",FACE,{"derivedFrom":[makeQuery(id+"F40.boolean.opBoolean","MERGE",FACE,{"derivedFrom":[makeQuery(id+"F38.boolean.opBoolean","MERGE",FACE,{"derivedFrom":[makeQuery(id+"F16.boolean.opBoolean","SPLIT",FACE,{"disambiguationData":[TD([makeQuery(id+"F8.boolean.opBoolean","COPY",FACE,{"derivedFrom":makeQuery(id+"F8.opExtrude","CAP_FACE",FACE,{"disambiguationData":[OSD([subQ3])],"isStart":false})})])],"derivedFrom":makeQuery(id+"F8.boolean.opBoolean","MERGE",FACE,{"derivedFrom":[makeQuery(id+"F7.opExtrude","CAP_FACE",FACE,{"disambiguationData":[OSD([subQ4,subQ2])],"isStart":false}),makeQuery(id+"F8.opExtrude","SWEPT_FACE",FACE,{"disambiguationData":[OSD([subQ3,subQ2])]})]})}),makeQuery(id+"F38.opExtrude","SWEPT_FACE",FACE,{"disambiguationData":[OSD([subQ4,subQ3,subQ2,subQ1,subQ0])]})]}),makeQuery(id+"F40.opExtrude","SWEPT_FACE",FACE,{"disambiguationData":[OSD([subQ4,subQ3,subQ2,subQ1,subQ0])]})]}),makeQuery(id+"F41.opExtrude","SWEPT_FACE",FACE,{"disambiguationData":[OSD([subQ4,subQ3,subQ2,subQ1,subQ0])]})]});}
            extrude(context, id + "F43", {"entities" : qUnion([Q0, Q1, Q2]), "operationType" : NewBodyOperationType.REMOVE, "oppositeDirection" : true, "depth" : 100 * mm, "offsetDistance" : 25 * mm});
        }
        {
            var Q0;
            {var subQ0=sQuery(id+"F15.wireOp",EDGE,"E5.left");var subQ1=sQuery(id+"F15.wireOp",EDGE,"E5.bottom");var subQ2=sQuery(id+"F10.wireOp",EDGE,"E2.right");var subQ6=sQuery(id+"F4.wireOp",EDGE,"E1.bottom");Q0=makeQuery(id+"F41.boolean.opBoolean","MERGE",FACE,{"derivedFrom":[makeQuery(id+"F37.boolean.opBoolean","MERGE",FACE,{"derivedFrom":[makeQuery(id+"F16.boolean.opBoolean","SPLIT",FACE,{"disambiguationData":[TD([makeQuery(id+"F6.boolean.opBoolean","COPY",FACE,{"derivedFrom":makeQuery(id+"F6.opExtrude","CAP_FACE",FACE,{"disambiguationData":[OSD([subQ6])],"isStart":false})})])],"derivedFrom":makeQuery(id+"F13.boolean.opBoolean","COPY",FACE,{"derivedFrom":makeQuery(id+"F13.opExtrude","CAP_FACE",FACE,{"disambiguationData":[OSD([subQ2])],"isStart":false})})}),makeQuery(id+"F37.opExtrude","SWEPT_FACE",FACE,{"disambiguationData":[OSD([subQ2,subQ1,subQ0])]})]}),makeQuery(id+"F41.opExtrude","SWEPT_FACE",FACE,{"disambiguationData":[OSD([subQ2,subQ1,subQ0])]})]});}
            var Q1;
            {var subQ0=sQuery(id+"F15.wireOp",EDGE,"E6.left");var subQ1=sQuery(id+"F15.wireOp",EDGE,"E6.bottom");var subQ2=sQuery(id+"F15.wireOp",EDGE,"E5.left");var subQ3=sQuery(id+"F15.wireOp",EDGE,"E5.top");var subQ4=sQuery(id+"F10.wireOp",EDGE,"E2.right");Q1=makeQuery(id+"F41.boolean.opBoolean","MERGE",FACE,{"derivedFrom":[makeQuery(id+"F35.boolean.opBoolean","MERGE",FACE,{"derivedFrom":[makeQuery(id+"F18.boolean.opBoolean","MERGE",FACE,{"derivedFrom":[makeQuery(id+"F16.boolean.opBoolean","SPLIT",FACE,{"disambiguationData":[TD([makeQuery(id+"F16.opExtrude","SWEPT_FACE",FACE,{"disambiguationData":[OSD([subQ3])]})])],"derivedFrom":makeQuery(id+"F13.boolean.opBoolean","COPY",FACE,{"derivedFrom":makeQuery(id+"F13.opExtrude","CAP_FACE",FACE,{"disambiguationData":[OSD([subQ4])],"isStart":false})})}),makeQuery(id+"F18.opExtrude","SWEPT_FACE",FACE,{"disambiguationData":[OSD([subQ4,subQ1,subQ0])]})]}),makeQuery(id+"F35.opExtrude","SWEPT_FACE",FACE,{"disambiguationData":[OSD([subQ4,subQ3,subQ2])]})]}),makeQuery(id+"F41.opExtrude","SWEPT_FACE",FACE,{"disambiguationData":[OSD([subQ4,subQ3,subQ2,subQ1,subQ0])]})]});}
            var Q2;
            {var subQ0=sQuery(id+"F15.wireOp",EDGE,"E6.left");var subQ1=sQuery(id+"F15.wireOp",EDGE,"E6.top");var subQ2=sQuery(id+"F10.wireOp",EDGE,"E2.right");var subQ3=sQuery(id+"F4.wireOp",EDGE,"E1.top");Q2=makeQuery(id+"F41.boolean.opBoolean","MERGE",FACE,{"derivedFrom":[makeQuery(id+"F40.boolean.opBoolean","MERGE",FACE,{"derivedFrom":[makeQuery(id+"F38.boolean.opBoolean","MERGE",FACE,{"derivedFrom":[makeQuery(id+"F16.boolean.opBoolean","SPLIT",FACE,{"disambiguationData":[TD([makeQuery(id+"F8.boolean.opBoolean","COPY",FACE,{"derivedFrom":makeQuery(id+"F8.opExtrude","CAP_FACE",FACE,{"disambiguationData":[OSD([subQ3])],"isStart":false})})])],"derivedFrom":makeQuery(id+"F13.boolean.opBoolean","COPY",FACE,{"derivedFrom":makeQuery(id+"F13.opExtrude","CAP_FACE",FACE,{"disambiguationData":[OSD([subQ2])],"isStart":false})})}),makeQuery(id+"F38.opExtrude","SWEPT_FACE",FACE,{"disambiguationData":[OSD([subQ2,subQ1,subQ0])]})]}),makeQuery(id+"F40.opExtrude","SWEPT_FACE",FACE,{"disambiguationData":[OSD([subQ2,subQ1,subQ0])]})]}),makeQuery(id+"F41.opExtrude","SWEPT_FACE",FACE,{"disambiguationData":[OSD([subQ2,subQ1,subQ0])]})]});}
            extrude(context, id + "F44", {"entities" : qUnion([Q0, Q1, Q2]), "operationType" : NewBodyOperationType.ADD, "depth" : 75 * mm, "offsetDistance" : 25 * mm});
        }
        {
            var Q0;
            {var subQ0=sQuery(id+"F14.wireOp",EDGE,"E4.right");var subQ1=sQuery(id+"F14.wireOp",EDGE,"E4.bottom");var subQ2=sQuery(id+"F14.wireOp",EDGE,"E3.right");var subQ3=sQuery(id+"F14.wireOp",EDGE,"E3.top");var subQ4=sQuery(id+"F10.wireOp",EDGE,"E2.left");Q0=makeQuery(id+"F41.boolean.opBoolean","MERGE",FACE,{"derivedFrom":[makeQuery(id+"F34.boolean.opBoolean","MERGE",FACE,{"derivedFrom":[makeQuery(id+"F32.boolean.opBoolean","MERGE",FACE,{"derivedFrom":[makeQuery(id+"F26.boolean.opBoolean","MERGE",FACE,{"derivedFrom":[makeQuery(id+"F24.boolean.opBoolean","MERGE",FACE,{"derivedFrom":[makeQuery(id+"F18.boolean.opBoolean","MERGE",FACE,{"derivedFrom":[makeQuery(id+"F16.boolean.opBoolean","SPLIT",FACE,{"disambiguationData":[TD([makeQuery(id+"F16.opExtrude","SWEPT_FACE",FACE,{"disambiguationData":[OSD([subQ3])]})])],"derivedFrom":makeQuery(id+"F12.boolean.opBoolean","COPY",FACE,{"derivedFrom":makeQuery(id+"F12.opExtrude","CAP_FACE",FACE,{"disambiguationData":[OSD([subQ4])],"isStart":false})})}),makeQuery(id+"F18.opExtrude","SWEPT_FACE",FACE,{"disambiguationData":[OSD([subQ4,subQ1,subQ0])]})]}),makeQuery(id+"F24.opExtrude","SWEPT_FACE",FACE,{"disambiguationData":[OSD([subQ4,subQ3,subQ2])]})]}),makeQuery(id+"F26.opExtrude","SWEPT_FACE",FACE,{"disambiguationData":[OSD([subQ4,subQ3,subQ2])]})]}),makeQuery(id+"F32.opExtrude","SWEPT_FACE",FACE,{"disambiguationData":[OSD([subQ4,subQ3,subQ2])]})]}),makeQuery(id+"F34.opExtrude","SWEPT_FACE",FACE,{"disambiguationData":[OSD([subQ4,subQ1,subQ0])]})]}),makeQuery(id+"F41.opExtrude","SWEPT_FACE",FACE,{"disambiguationData":[OSD([subQ4,subQ3,subQ2,subQ1,subQ0])]})]});}
            var Q1;
            {var subQ0=sQuery(id+"F14.wireOp",EDGE,"E4.right");var subQ1=sQuery(id+"F14.wireOp",EDGE,"E4.top");var subQ2=sQuery(id+"F10.wireOp",EDGE,"E2.left");var subQ3=sQuery(id+"F4.wireOp",EDGE,"E1.top");Q1=makeQuery(id+"F41.boolean.opBoolean","MERGE",FACE,{"derivedFrom":[makeQuery(id+"F28.boolean.opBoolean","MERGE",FACE,{"derivedFrom":[makeQuery(id+"F22.boolean.opBoolean","MERGE",FACE,{"derivedFrom":[makeQuery(id+"F16.boolean.opBoolean","SPLIT",FACE,{"disambiguationData":[TD([makeQuery(id+"F8.boolean.opBoolean","COPY",FACE,{"derivedFrom":makeQuery(id+"F8.opExtrude","CAP_FACE",FACE,{"disambiguationData":[OSD([subQ3])],"isStart":false})})])],"derivedFrom":makeQuery(id+"F12.boolean.opBoolean","COPY",FACE,{"derivedFrom":makeQuery(id+"F12.opExtrude","CAP_FACE",FACE,{"disambiguationData":[OSD([subQ2])],"isStart":false})})}),makeQuery(id+"F22.opExtrude","SWEPT_FACE",FACE,{"disambiguationData":[OSD([subQ2,subQ1,subQ0])]})]}),makeQuery(id+"F28.opExtrude","SWEPT_FACE",FACE,{"disambiguationData":[OSD([subQ2,subQ1,subQ0])]})]}),makeQuery(id+"F41.opExtrude","SWEPT_FACE",FACE,{"disambiguationData":[OSD([subQ2,subQ1,subQ0])]})]});}
            var Q2;
            {var subQ0=sQuery(id+"F14.wireOp",EDGE,"E3.right");var subQ1=sQuery(id+"F14.wireOp",EDGE,"E3.bottom");var subQ2=sQuery(id+"F10.wireOp",EDGE,"E2.left");var subQ6=sQuery(id+"F4.wireOp",EDGE,"E1.bottom");Q2=makeQuery(id+"F41.boolean.opBoolean","MERGE",FACE,{"derivedFrom":[makeQuery(id+"F30.boolean.opBoolean","MERGE",FACE,{"derivedFrom":[makeQuery(id+"F20.boolean.opBoolean","MERGE",FACE,{"derivedFrom":[makeQuery(id+"F16.boolean.opBoolean","SPLIT",FACE,{"disambiguationData":[TD([makeQuery(id+"F6.boolean.opBoolean","COPY",FACE,{"derivedFrom":makeQuery(id+"F6.opExtrude","CAP_FACE",FACE,{"disambiguationData":[OSD([subQ6])],"isStart":false})})])],"derivedFrom":makeQuery(id+"F12.boolean.opBoolean","COPY",FACE,{"derivedFrom":makeQuery(id+"F12.opExtrude","CAP_FACE",FACE,{"disambiguationData":[OSD([subQ2])],"isStart":false})})}),makeQuery(id+"F20.opExtrude","SWEPT_FACE",FACE,{"disambiguationData":[OSD([subQ2,subQ1,subQ0])]})]}),makeQuery(id+"F30.opExtrude","SWEPT_FACE",FACE,{"disambiguationData":[OSD([subQ2,subQ1,subQ0])]})]}),makeQuery(id+"F41.opExtrude","SWEPT_FACE",FACE,{"disambiguationData":[OSD([subQ2,subQ1,subQ0])]})]});}
            extrude(context, id + "F45", {"entities" : qUnion([Q0, Q1, Q2]), "operationType" : NewBodyOperationType.REMOVE, "oppositeDirection" : true, "depth" : 50 * mm, "offsetDistance" : 25 * mm});
        }
        {
            var Q0;
            Q0=makeQuery(id+"F44.opExtrude","CAP_FACE",FACE,{"disambiguationData":[OSD([sQuery(id+"F10.wireOp",EDGE,"E2.right"),sQuery(id+"F15.wireOp",EDGE,"E5.bottom"),sQuery(id+"F15.wireOp",EDGE,"E5.left")])],"isStart":false});
            var Q1;
            Q1=makeQuery(id+"F44.opExtrude","CAP_FACE",FACE,{"disambiguationData":[OSD([sQuery(id+"F10.wireOp",EDGE,"E2.right"),sQuery(id+"F15.wireOp",EDGE,"E5.top"),sQuery(id+"F15.wireOp",EDGE,"E5.left"),sQuery(id+"F15.wireOp",EDGE,"E6.bottom"),sQuery(id+"F15.wireOp",EDGE,"E6.left")])],"isStart":false});
            var Q2;
            Q2=makeQuery(id+"F44.opExtrude","CAP_FACE",FACE,{"disambiguationData":[OSD([sQuery(id+"F10.wireOp",EDGE,"E2.right"),sQuery(id+"F15.wireOp",EDGE,"E6.top"),sQuery(id+"F15.wireOp",EDGE,"E6.left")])],"isStart":false});
            extrude(context, id + "F46", {"entities" : qUnion([Q0, Q1, Q2]), "operationType" : NewBodyOperationType.REMOVE, "oppositeDirection" : true, "depth" : 25 * mm, "offsetDistance" : 25 * mm});
        }
        {
            var Q0;
            {var subQ0=sQuery(id+"F15.wireOp",EDGE,"E6.left");var subQ1=sQuery(id+"F15.wireOp",EDGE,"E6.top");var subQ2=sQuery(id+"F10.wireOp",EDGE,"E2.right");var subQ3=makeQuery(id+"F17.opExtrude","CAP_VERTEX",VERTEX,{"disambiguationData":[OSD([subQ2,subQ1,subQ0]),TDD([makeQuery(id+"F16.opExtrude","CAP_VERTEX",VERTEX,{"disambiguationData":[OSD([subQ2,subQ1,subQ0])],"isStart":false})])],"isStart":false});var subQ5=sQuery(id+"F10.wireOp",EDGE,"E2.top");var subQ6=sQuery(id+"F10.wireOp",EDGE,"E2.bottom");var subQ7=makeQuery(id+"F11.opExtrude","CAP_FACE",FACE,{"disambiguationData":[OSD([subQ6,subQ5,sQuery(id+"F10.wireOp",EDGE,"E2.left"),subQ2])],"isStart":false});var subQ8=sQuery(id+"F0.wireOp",EDGE,"E0.left");var subQ9=makeQuery(id+"F1.opExtrude","CAP_EDGE",EDGE,{"disambiguationData":[OSD([subQ8])],"isStart":false});var subQ10=makeQuery(id+"F2.opExtrude","SWEPT_FACE",FACE,{"disambiguationData":[OSD([subQ8]),TDD([subQ9])]});var subQ11=sQuery(id+"F14.wireOp",EDGE,"E3.top");var subQ12=sQuery(id+"F14.wireOp",EDGE,"E3.bottom");var subQ13=makeQuery(id+"F16.opExtrude","CAP_FACE",FACE,{"disambiguationData":[OSD([subQ12,subQ11,sQuery(id+"F14.wireOp",EDGE,"E3.left"),sQuery(id+"F14.wireOp",EDGE,"E3.right")])],"isStart":false});var subQ14=sQuery(id+"F4.wireOp",EDGE,"E1.top");var subQ15=sQuery(id+"F4.wireOp",EDGE,"E1.left");var subQ16=sQuery(id+"F4.wireOp",EDGE,"E1.bottom");var subQ17=makeQuery(id+"F9.opExtrude","SWEPT_FACE",FACE,{"disambiguationData":[OSD([subQ16,subQ14,subQ15]),TDD([makeQuery(id+"F8.boolean.opBoolean","MERGE",EDGE,{"derivedFrom":[makeQuery(id+"F6.boolean.opBoolean","MERGE",EDGE,{"derivedFrom":[makeQuery(id+"F5.boolean.opBoolean","COPY",EDGE,{"derivedFrom":makeQuery(id+"F5.opExtrude","CAP_EDGE",EDGE,{"disambiguationData":[OSD([subQ15])],"isStart":true})}),makeQuery(id+"F6.opExtrude","SWEPT_EDGE",EDGE,{"disambiguationData":[OSD([subQ16,subQ15]),TDD([makeQuery(id+"F5.boolean.opBoolean","COPY",VERTEX,{"derivedFrom":makeQuery(id+"F5.opExtrude","CAP_VERTEX",VERTEX,{"disambiguationData":[OSD([subQ16,subQ15])],"isStart":true})})])]})]}),makeQuery(id+"F8.opExtrude","SWEPT_EDGE",EDGE,{"disambiguationData":[OSD([subQ14,subQ15]),TDD([makeQuery(id+"F5.boolean.opBoolean","COPY",VERTEX,{"derivedFrom":makeQuery(id+"F5.opExtrude","CAP_VERTEX",VERTEX,{"disambiguationData":[OSD([subQ14,subQ15])],"isStart":true})})])]})]})])]});var subQ18=sQuery(id+"F0.wireOp",EDGE,"E0.bottom");var subQ19=makeQuery(id+"F1.opExtrude","CAP_FACE",FACE,{"disambiguationData":[OSD([subQ18,sQuery(id+"F0.wireOp",EDGE,"E0.top"),subQ8,sQuery(id+"F0.wireOp",EDGE,"E0.right")])],"isStart":false});var subQ20=sQuery(id+"F4.wireOp",EDGE,"E1.right");var subQ21=makeQuery(id+"F7.opExtrude","SWEPT_FACE",FACE,{"disambiguationData":[OSD([subQ16,subQ20]),TDD([makeQuery(id+"F6.boolean.opBoolean","MERGE",EDGE,{"derivedFrom":[makeQuery(id+"F5.boolean.opBoolean","COPY",EDGE,{"derivedFrom":makeQuery(id+"F5.opExtrude","CAP_EDGE",EDGE,{"disambiguationData":[OSD([subQ20])],"isStart":true})}),makeQuery(id+"F6.opExtrude","SWEPT_EDGE",EDGE,{"disambiguationData":[OSD([subQ16,subQ20]),TDD([makeQuery(id+"F5.boolean.opBoolean","COPY",VERTEX,{"derivedFrom":makeQuery(id+"F5.opExtrude","CAP_VERTEX",VERTEX,{"disambiguationData":[OSD([subQ16,subQ20])],"isStart":true})})])]})]})])]});var subQ22=makeQuery(id+"F1.opExtrude","CAP_VERTEX",VERTEX,{"disambiguationData":[OSD([subQ18,subQ8])],"isStart":false});var subQ23=makeQuery(id+"F3.opExtrude","SWEPT_FACE",FACE,{"disambiguationData":[OSD([subQ18,subQ8]),TDD([makeQuery(id+"F2.boolean.opBoolean","MERGE",EDGE,{"derivedFrom":[makeQuery(id+"F1.opExtrude","CAP_EDGE",EDGE,{"disambiguationData":[OSD([subQ18])],"isStart":false}),makeQuery(id+"F2.opExtrude","SWEPT_EDGE",EDGE,{"disambiguationData":[OSD([subQ18,subQ8]),TDD([subQ22])]})]})])]});var subQ24=sQuery(id+"F14.wireOp",EDGE,"E4.top");var subQ25=sQuery(id+"F14.wireOp",EDGE,"E4.bottom");var subQ26=makeQuery(id+"F16.opExtrude","CAP_FACE",FACE,{"disambiguationData":[OSD([subQ25,subQ24,sQuery(id+"F14.wireOp",EDGE,"E4.left"),sQuery(id+"F14.wireOp",EDGE,"E4.right")])],"isStart":false});var subQ27=sQuery(id+"F15.wireOp",EDGE,"E5.left");var subQ28=sQuery(id+"F15.wireOp",EDGE,"E5.top");var subQ29=sQuery(id+"F15.wireOp",EDGE,"E5.bottom");var subQ30=makeQuery(id+"F16.opExtrude","CAP_FACE",FACE,{"disambiguationData":[OSD([subQ29,subQ28,subQ27,sQuery(id+"F15.wireOp",EDGE,"E5.right")])],"isStart":false});var subQ31=sQuery(id+"F15.wireOp",EDGE,"E6.bottom");var subQ32=makeQuery(id+"F16.opExtrude","CAP_FACE",FACE,{"disambiguationData":[OSD([subQ31,subQ1,subQ0,sQuery(id+"F15.wireOp",EDGE,"E6.right")])],"isStart":false});var subQ33=makeQuery(id+"F13.boolean.opBoolean","COPY",EDGE,{"derivedFrom":makeQuery(id+"F13.opExtrude","CAP_EDGE",EDGE,{"disambiguationData":[OSD([subQ2]),TDD([makeQuery(id+"F11.opExtrude","CAP_EDGE",EDGE,{"disambiguationData":[OSD([subQ2])],"isStart":false})])],"isStart":false})});var subQ34=makeQuery(id+"F16.opExtrude","CAP_EDGE",EDGE,{"disambiguationData":[OSD([subQ24])],"isStart":false});var subQ35=makeQuery(id+"F22.boolean.opBoolean","COPY",EDGE,{"derivedFrom":makeQuery(id+"F22.opExtrude","CAP_EDGE",EDGE,{"disambiguationData":[OSD([subQ24]),TDD([makeQuery(id+"F17.opExtrude","CAP_EDGE",EDGE,{"disambiguationData":[OSD([subQ24]),TDD([subQ34])],"isStart":false})])],"isStart":false})});var subQ36=makeQuery(id+"F20.boolean.opBoolean","COPY",EDGE,{"derivedFrom":makeQuery(id+"F20.opExtrude","CAP_EDGE",EDGE,{"disambiguationData":[OSD([subQ12]),TDD([makeQuery(id+"F16.opExtrude","CAP_EDGE",EDGE,{"disambiguationData":[OSD([subQ12])],"isStart":false})])],"isStart":false})});var subQ37=makeQuery(id+"F23.opExtrude","CAP_EDGE",EDGE,{"disambiguationData":[OSD([subQ12]),TDD([subQ36])],"isStart":false});var subQ38=makeQuery(id+"F16.opExtrude","CAP_EDGE",EDGE,{"disambiguationData":[OSD([subQ11])],"isStart":false});Q0=makeQuery(id+"F44.boolean.opBoolean","MERGE",FACE,{"derivedFrom":[makeQuery(id+"F42.boolean.opBoolean","MERGE",FACE,{"derivedFrom":[makeQuery(id+"F39.boolean.opBoolean","MERGE",FACE,{"derivedFrom":[makeQuery(id+"F36.boolean.opBoolean","MERGE",FACE,{"derivedFrom":[makeQuery(id+"F33.boolean.opBoolean","MERGE",FACE,{"derivedFrom":[makeQuery(id+"F31.boolean.opBoolean","MERGE",FACE,{"derivedFrom":[makeQuery(id+"F29.boolean.opBoolean","MERGE",FACE,{"derivedFrom":[makeQuery(id+"F27.boolean.opBoolean","MERGE",FACE,{"derivedFrom":[makeQuery(id+"F25.boolean.opBoolean","MERGE",FACE,{"derivedFrom":[makeQuery(id+"F23.boolean.opBoolean","MERGE",FACE,{"derivedFrom":[makeQuery(id+"F21.boolean.opBoolean","MERGE",FACE,{"derivedFrom":[makeQuery(id+"F19.boolean.opBoolean","MERGE",FACE,{"derivedFrom":[makeQuery(id+"F17.boolean.opBoolean","MERGE",FACE,{"derivedFrom":[makeQuery(id+"F16.boolean.opBoolean","MERGE",FACE,{"derivedFrom":[makeQuery(id+"F11.boolean.opBoolean","MERGE",FACE,{"derivedFrom":[makeQuery(id+"F9.boolean.opBoolean","MERGE",FACE,{"derivedFrom":[makeQuery(id+"F7.boolean.opBoolean","MERGE",FACE,{"derivedFrom":[makeQuery(id+"F3.boolean.opBoolean","MERGE",FACE,{"derivedFrom":[makeQuery(id+"F2.boolean.opBoolean","MERGE",FACE,{"derivedFrom":[subQ19,subQ10]}),subQ23]}),subQ21]}),subQ17]}),subQ7]}),subQ13,subQ26,subQ30,subQ32]}),makeQuery(id+"F17.opExtrude","SWEPT_FACE",FACE,{"disambiguationData":[OSD([subQ24]),TDD([subQ34])]}),makeQuery(id+"F17.opExtrude","SWEPT_FACE",FACE,{"disambiguationData":[OSD([subQ1]),TDD([makeQuery(id+"F16.opExtrude","CAP_EDGE",EDGE,{"disambiguationData":[OSD([subQ1])],"isStart":false})])]})]}),makeQuery(id+"F19.opExtrude","SWEPT_FACE",FACE,{"disambiguationData":[OSD([subQ11]),TDD([subQ38])]})]}),makeQuery(id+"F21.opExtrude","SWEPT_FACE",FACE,{"disambiguationData":[OSD([subQ25]),TDD([makeQuery(id+"F18.boolean.opBoolean","COPY",EDGE,{"derivedFrom":makeQuery(id+"F18.opExtrude","CAP_EDGE",EDGE,{"disambiguationData":[OSD([subQ25]),TDD([makeQuery(id+"F16.opExtrude","CAP_EDGE",EDGE,{"disambiguationData":[OSD([subQ25])],"isStart":false})])],"isStart":false})})])]})]}),makeQuery(id+"F23.opExtrude","SWEPT_FACE",FACE,{"disambiguationData":[OSD([subQ12]),TDD([subQ36])]})]}),makeQuery(id+"F25.opExtrude","SWEPT_FACE",FACE,{"disambiguationData":[OSD([subQ12]),TDD([subQ37])]})]}),makeQuery(id+"F27.opExtrude","SWEPT_FACE",FACE,{"disambiguationData":[OSD([subQ24]),TDD([subQ35])]})]}),makeQuery(id+"F29.opExtrude","SWEPT_FACE",FACE,{"disambiguationData":[OSD([subQ11]),TDD([makeQuery(id+"F26.boolean.opBoolean","COPY",EDGE,{"derivedFrom":makeQuery(id+"F26.opExtrude","CAP_EDGE",EDGE,{"disambiguationData":[OSD([subQ11]),TDD([makeQuery(id+"F24.boolean.opBoolean","COPY",EDGE,{"derivedFrom":makeQuery(id+"F24.opExtrude","CAP_EDGE",EDGE,{"disambiguationData":[OSD([subQ11]),TDD([makeQuery(id+"F19.opExtrude","CAP_EDGE",EDGE,{"disambiguationData":[OSD([subQ11]),TDD([subQ38])],"isStart":false})])],"isStart":false})})])],"isStart":false})})])]})]}),makeQuery(id+"F31.opExtrude","SWEPT_FACE",FACE,{"disambiguationData":[OSD([subQ12]),TDD([makeQuery(id+"F30.boolean.opBoolean","COPY",EDGE,{"derivedFrom":makeQuery(id+"F30.opExtrude","CAP_EDGE",EDGE,{"disambiguationData":[OSD([subQ12]),TDD([makeQuery(id+"F25.opExtrude","CAP_EDGE",EDGE,{"disambiguationData":[OSD([subQ12]),TDD([subQ37])],"isStart":false})])],"isStart":false})})])]})]}),makeQuery(id+"F33.opExtrude","SWEPT_FACE",FACE,{"disambiguationData":[OSD([subQ24]),TDD([makeQuery(id+"F28.boolean.opBoolean","COPY",EDGE,{"derivedFrom":makeQuery(id+"F28.opExtrude","CAP_EDGE",EDGE,{"disambiguationData":[OSD([subQ24]),TDD([makeQuery(id+"F27.opExtrude","CAP_EDGE",EDGE,{"disambiguationData":[OSD([subQ24]),TDD([subQ35])],"isStart":false})])],"isStart":false})})])]})]}),makeQuery(id+"F36.opExtrude","SWEPT_FACE",FACE,{"disambiguationData":[OSD([subQ28]),TDD([makeQuery(id+"F35.boolean.opBoolean","COPY",EDGE,{"derivedFrom":makeQuery(id+"F35.opExtrude","CAP_EDGE",EDGE,{"disambiguationData":[OSD([subQ28]),TDD([makeQuery(id+"F16.opExtrude","CAP_EDGE",EDGE,{"disambiguationData":[OSD([subQ28])],"isStart":false})])],"isStart":false})})])]})]}),makeQuery(id+"F39.opExtrude","SWEPT_FACE",FACE,{"disambiguationData":[OSD([subQ31]),TDD([makeQuery(id+"F18.boolean.opBoolean","COPY",EDGE,{"derivedFrom":makeQuery(id+"F18.opExtrude","CAP_EDGE",EDGE,{"disambiguationData":[OSD([subQ31]),TDD([makeQuery(id+"F16.opExtrude","CAP_EDGE",EDGE,{"disambiguationData":[OSD([subQ31])],"isStart":false})])],"isStart":false})})])]})]}),makeQuery(id+"F42.opExtrude","SWEPT_FACE",FACE,{"disambiguationData":[OSD([subQ18,subQ8]),TDD([makeQuery(id+"F3.boolean.opBoolean","MERGE",EDGE,{"derivedFrom":[makeQuery(id+"F2.opExtrude","CAP_EDGE",EDGE,{"disambiguationData":[OSD([subQ8]),TDD([subQ9])],"isStart":false}),makeQuery(id+"F3.opExtrude","SWEPT_EDGE",EDGE,{"disambiguationData":[OSD([subQ18,subQ8]),TDD([makeQuery(id+"F2.opExtrude","CAP_VERTEX",VERTEX,{"disambiguationData":[OSD([subQ18,subQ8]),TDD([subQ22])],"isStart":false})])]})]})])]})]}),makeQuery(id+"F44.opExtrude","SWEPT_FACE",FACE,{"disambiguationData":[OSD([subQ2,subQ29,subQ27]),TDD([makeQuery(id+"F37.boolean.opBoolean","MERGE",EDGE,{"derivedFrom":[makeQuery(id+"F16.boolean.opBoolean","SPLIT",EDGE,{"disambiguationData":[TD([makeQuery(id+"F6.boolean.opBoolean","COPY",FACE,{"derivedFrom":makeQuery(id+"F6.opExtrude","CAP_FACE",FACE,{"disambiguationData":[OSD([subQ16])],"isStart":false})})])],"derivedFrom":subQ33}),makeQuery(id+"F37.opExtrude","SWEPT_EDGE",EDGE,{"disambiguationData":[OSD([subQ2,subQ29,subQ27]),TDD([makeQuery(id+"F16.opExtrude","CAP_VERTEX",VERTEX,{"disambiguationData":[OSD([subQ2,subQ29,subQ27])],"isStart":false})])]})]})])]}),makeQuery(id+"F44.opExtrude","SWEPT_FACE",FACE,{"disambiguationData":[OSD([subQ2,subQ28,subQ27,subQ31,subQ0]),TDD([makeQuery(id+"F35.boolean.opBoolean","MERGE",EDGE,{"derivedFrom":[makeQuery(id+"F18.boolean.opBoolean","MERGE",EDGE,{"derivedFrom":[makeQuery(id+"F16.boolean.opBoolean","SPLIT",EDGE,{"disambiguationData":[TD([makeQuery(id+"F16.opExtrude","SWEPT_FACE",FACE,{"disambiguationData":[OSD([subQ28])]})])],"derivedFrom":subQ33}),makeQuery(id+"F18.opExtrude","SWEPT_EDGE",EDGE,{"disambiguationData":[OSD([subQ2,subQ31,subQ0]),TDD([makeQuery(id+"F16.opExtrude","CAP_VERTEX",VERTEX,{"disambiguationData":[OSD([subQ2,subQ31,subQ0])],"isStart":false})])]})]}),makeQuery(id+"F35.opExtrude","SWEPT_EDGE",EDGE,{"disambiguationData":[OSD([subQ2,subQ28,subQ27]),TDD([makeQuery(id+"F16.opExtrude","CAP_VERTEX",VERTEX,{"disambiguationData":[OSD([subQ2,subQ28,subQ27])],"isStart":false})])]})]})])]}),makeQuery(id+"F44.opExtrude","SWEPT_FACE",FACE,{"disambiguationData":[OSD([subQ2,subQ1,subQ0]),TDD([makeQuery(id+"F40.boolean.opBoolean","MERGE",EDGE,{"derivedFrom":[makeQuery(id+"F38.boolean.opBoolean","MERGE",EDGE,{"derivedFrom":[makeQuery(id+"F16.boolean.opBoolean","SPLIT",EDGE,{"disambiguationData":[TD([makeQuery(id+"F8.boolean.opBoolean","COPY",FACE,{"derivedFrom":makeQuery(id+"F8.opExtrude","CAP_FACE",FACE,{"disambiguationData":[OSD([subQ14])],"isStart":false})})])],"derivedFrom":subQ33}),makeQuery(id+"F38.opExtrude","SWEPT_EDGE",EDGE,{"disambiguationData":[OSD([subQ2,subQ1,subQ0]),TDD([subQ3])]})]}),makeQuery(id+"F40.opExtrude","SWEPT_EDGE",EDGE,{"disambiguationData":[OSD([subQ2,subQ1,subQ0]),TDD([makeQuery(id+"F38.boolean.opBoolean","COPY",VERTEX,{"derivedFrom":makeQuery(id+"F38.opExtrude","CAP_VERTEX",VERTEX,{"disambiguationData":[OSD([subQ2,subQ1,subQ0]),TDD([subQ3])],"isStart":false})})])]})]})])]})]});}
            fillet(context, id + "F47", {"entities" : qUnion([Q0]), "radius" : 3 * mm, "tangentPropagation" : true, "allowEdgeOverflow" : false});
        }
    });
